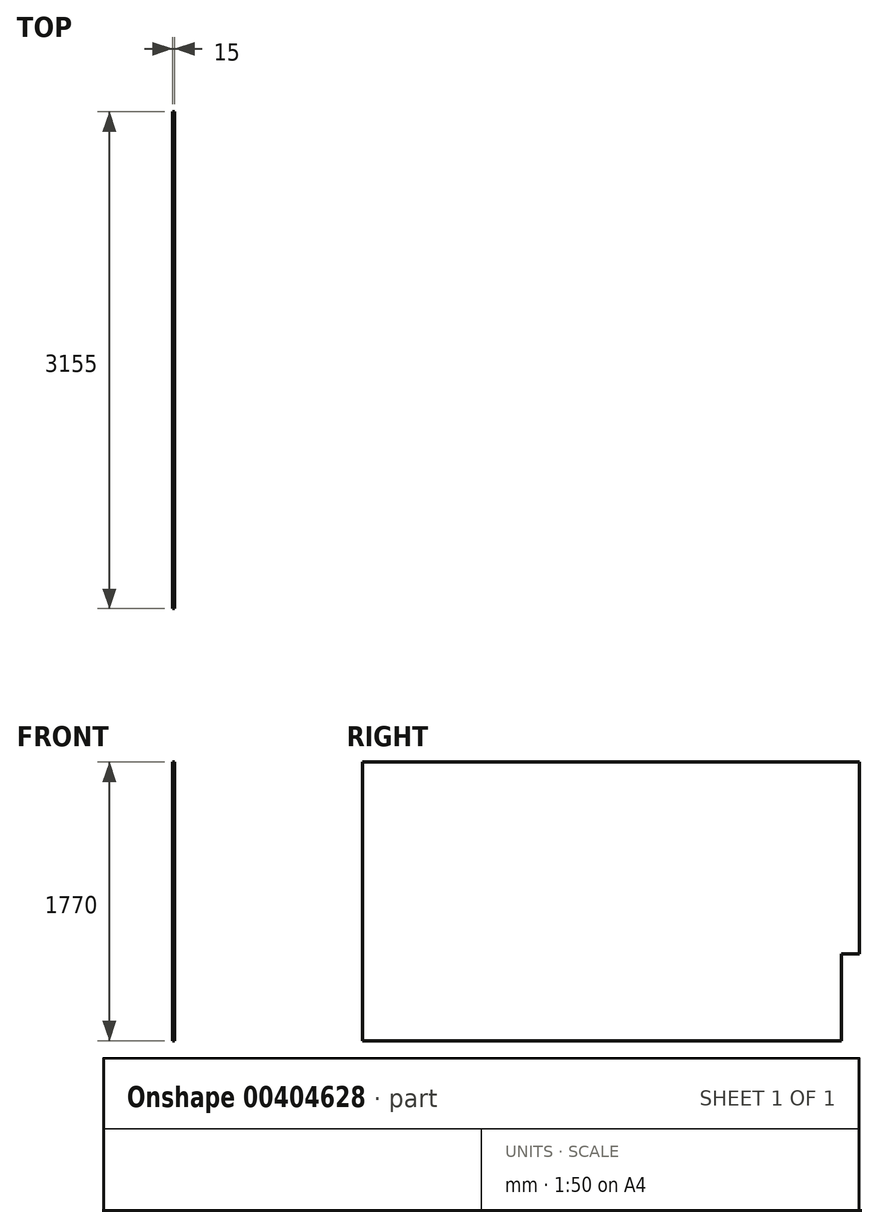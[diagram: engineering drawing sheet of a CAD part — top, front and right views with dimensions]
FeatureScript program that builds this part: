
annotation { "Feature Type Name" : "Feature", "Feature Type Description" : "" }
export const myFeature = defineFeature(function(context is Context, id is Id, definition is map)
    precondition{}
    {
        {
            var Q0;
            Q0=qCreatedBy(makeId("Right.planeOp"),FACE);
            var sketch = newSketch(context, id + "F0", { "sketchPlane" : qUnion([Q0])});
            skLineSegment(sketch, "E0", {"start": v(-1577.5, 885) * mm, "end": v(1577.5, 885) * mm});
            skLineSegment(sketch, "E1", {"start": v(1577.5, 885) * mm, "end": v(1577.5, -335) * mm});
            skLineSegment(sketch, "E2", {"start": v(1577.5, -335) * mm, "end": v(1462.5, -335) * mm});
            skLineSegment(sketch, "E3", {"start": v(1462.5, -335) * mm, "end": v(1462.5, -885) * mm});
            skLineSegment(sketch, "E4", {"start": v(1462.5, -885) * mm, "end": v(-1577.5, -885) * mm});
            skLineSegment(sketch, "E5", {"start": v(-1577.5, -885) * mm, "end": v(-1577.5, 885) * mm});
            skSolve(sketch);
        }
        {
            var Q0;
            Q0=makeQuery(id+"F0.imprint","IMPRINT",FACE,{"disambiguationData":[TD([[makeQuery(id+"F0.imprint","IMPRINT",EDGE,{"derivedFrom":sQuery(id+"F0.wireOp",EDGE,"E0")}),-1.0]])]});
            extrude(context, id + "F1", {"entities" : qUnion([Q0]), "depth" : 15 * mm});
        }
    });
